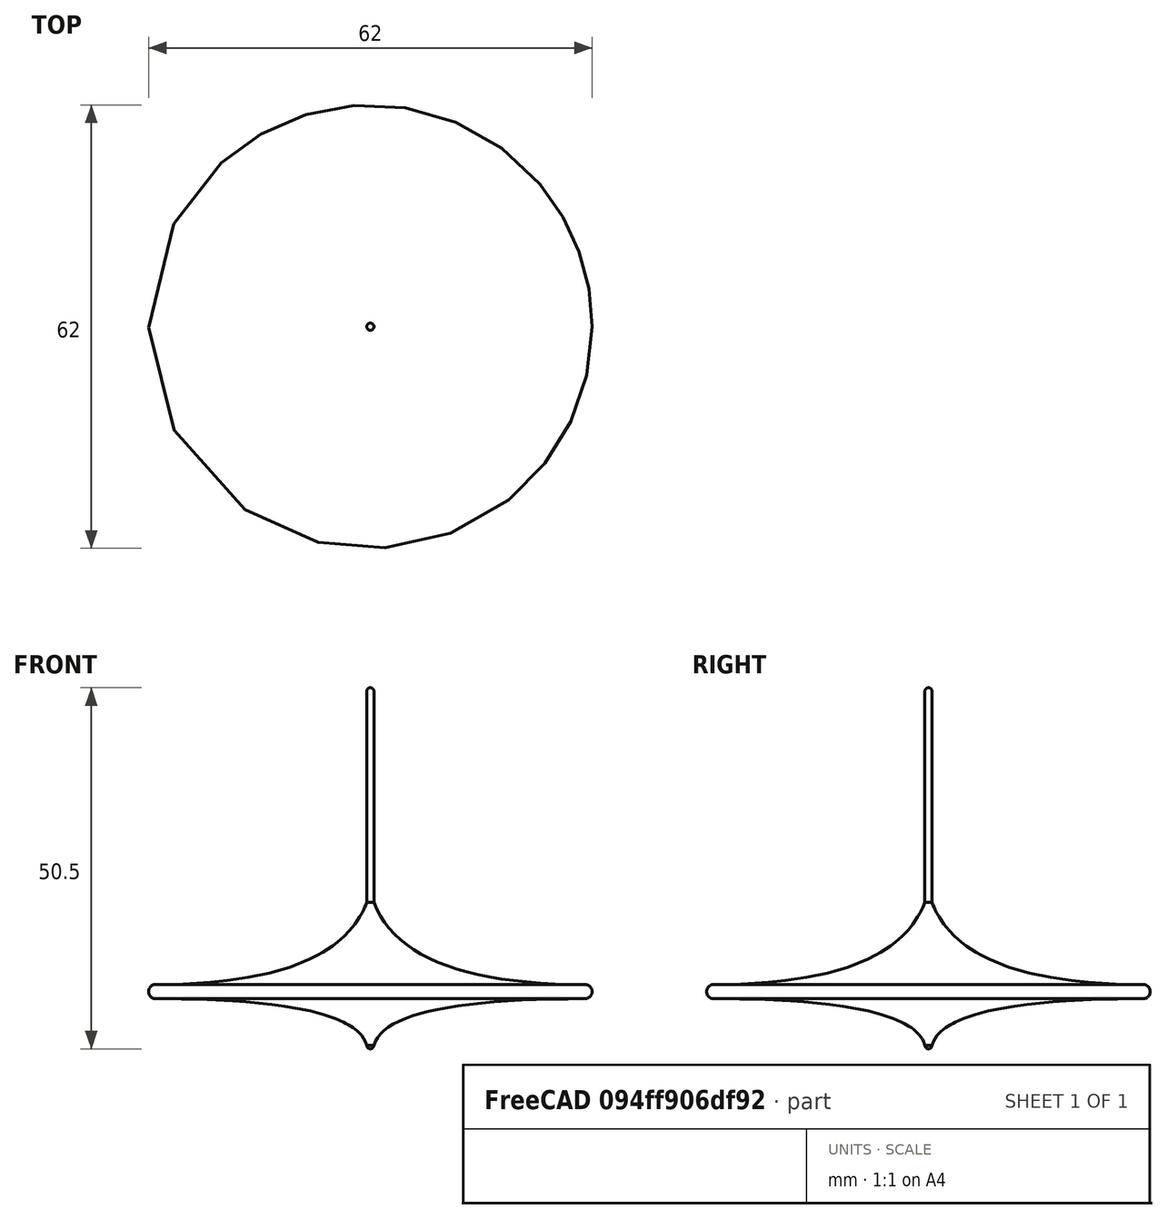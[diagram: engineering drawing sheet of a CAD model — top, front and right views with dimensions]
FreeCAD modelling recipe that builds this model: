
FCSTD DOCUMENT  (FreeCAD 0.21R33694 (Git))
Label: top_2
License: All rights reserved
LicenseURL: https://en.wikipedia.org/wiki/All_rights_reserved
objects: Sketcher::SketchObject×1, PartDesign::Revolution×1, PartDesign::Body×1
note: 4 computed .brp shape members not serialized (recipe doc carries the construction recipe); baked Part::Feature solids carry a one-line shape summary decoded from their .brp

FEATURE [Sketcher::SketchObject] Sketch
  FullyConstrained = false
  MapMode = 5
  Placement = pos=(0,0,0) rot=(1,0,0;1.5708rad)
  Support = -> [XZ_Plane]
  sketch-geometry (19):
    g0: ArcOfCircle CenterX=0 CenterY=0 CenterZ=0 NormalX=0 NormalY=0 NormalZ=1 AngleXU=0 Radius=0.5 StartAngle=4.71239 EndAngle=6.28319
    g1: GeomPoint X=30 Y=7.5 Z=0
    g2: ArcOfCircle CenterX=30 CenterY=7.5 CenterZ=0 NormalX=0 NormalY=0 NormalZ=1 AngleXU=0 Radius=1 StartAngle=4.71239 EndAngle=7.85398
    g3: Circle CenterX=0.5 CenterY=0 CenterZ=0 NormalX=0 NormalY=0 NormalZ=1 AngleXU=0 Radius=1
    g4: Circle CenterX=2.29683 CenterY=6.5 CenterZ=0 NormalX=0 NormalY=0 NormalZ=1 AngleXU=0 Radius=1
    g5: Circle CenterX=30 CenterY=6.5 CenterZ=0 NormalX=0 NormalY=0 NormalZ=1 AngleXU=0 Radius=1
    g6: BSplineCurve PolesCount=3 KnotsCount=2 Degree=2 IsPeriodic=0
    g7: GeomPoint X=0.5 Y=0 Z=0
    g8: GeomPoint X=30 Y=6.5 Z=0
    g9: GeomPoint X=0 Y=49.5 Z=0
    g10: ArcOfCircle CenterX=0 CenterY=49.5 CenterZ=0 NormalX=0 NormalY=0 NormalZ=1 AngleXU=0 Radius=0.5 StartAngle=0 EndAngle=1.5708
    g11: LineSegment StartX=0 StartY=-0.5 StartZ=0 EndX=0 EndY=50 EndZ=0
    g12: LineSegment StartX=0.5 StartY=49.5 StartZ=0 EndX=0.5 EndY=20 EndZ=0
    g13: Circle CenterX=0.5 CenterY=20 CenterZ=0 NormalX=0 NormalY=0 NormalZ=1 AngleXU=0 Radius=1
    g14: Circle CenterX=4.83168 CenterY=8.5 CenterZ=0 NormalX=0 NormalY=0 NormalZ=1 AngleXU=0 Radius=1
    g15: Circle CenterX=30 CenterY=8.5 CenterZ=0 NormalX=0 NormalY=0 NormalZ=1 AngleXU=0 Radius=1
    g16: BSplineCurve PolesCount=3 KnotsCount=2 Degree=2 IsPeriodic=0
    g17: GeomPoint X=0.5 Y=20 Z=0
    g18: GeomPoint X=30 Y=8.5 Z=0
  constraints (43):
    c: Coincident(g0,g-1)
    c: PointOnObject(g0,g-1)
    c: PointOnObject(g0,g-2)
    c: DistanceY(g0,g0) = 0.5
    c: DistanceY(g0,g1) = 7.5
    c: DistanceX(g0,g1) = 30
    c: Coincident(g2,g1)
    c: Vertical(g2,g2)
    c: Vertical(g2,g2)
    c: DistanceY(g2,g2) = 1
    c: Weight(g3) = 1
    c: Coincident(g6,g0)
    c: Equal(g3,g4)
    c: Equal(g3,g5)
    c: Coincident(g6,g2)
    c: InternalAlignment(g3,g6)
    c: InternalAlignment(g4,g6)
    c: InternalAlignment(g5,g6)
    c: InternalAlignment(g7,g6)
    c: InternalAlignment(g8,g6)
    c: Vertical(g9,g0)
    c: Coincident(g10,g9)
    c: Horizontal(g10,g10)
    c: Vertical(g10,g10)
    c: Equal(g10,g0)
    c: DistanceY(g0,g10) = 50
    c: Coincident(g11,g0)
    c: Coincident(g11,g10)
    c: Horizontal(g4,g2)
    c: Coincident(g12,g10)
    c: Vertical(g12)
    c: DistanceY(g12,g10) = 30
    c: Weight(g13) = 1
    c: Coincident(g16,g12)
    c: Equal(g13,g14)
    c: Equal(g13,g15)
    c: Coincident(g16,g2)
    c: InternalAlignment(g13,g16)
    c: InternalAlignment(g14,g16)
    c: InternalAlignment(g15,g16)
    c: InternalAlignment(g17,g16)
    c: InternalAlignment(g18,g16)
    c: Horizontal(g14,g2)
FEATURE [PartDesign::Revolution] Revolution
  Angle = 360
  Axis = (0,2e-16,1)
  Base = (0,0,0)
  Placement = pos=(0,0,0) rot=(1,0,0;1.5708rad)
  Profile = -> Sketch
  ReferenceAxis = -> Sketch [V_Axis]
  Reversed = true
FEATURE [PartDesign::Body] Body
  Group = -> [Sketch,Revolution]
  Origin = -> Origin
  Tip = -> Revolution
